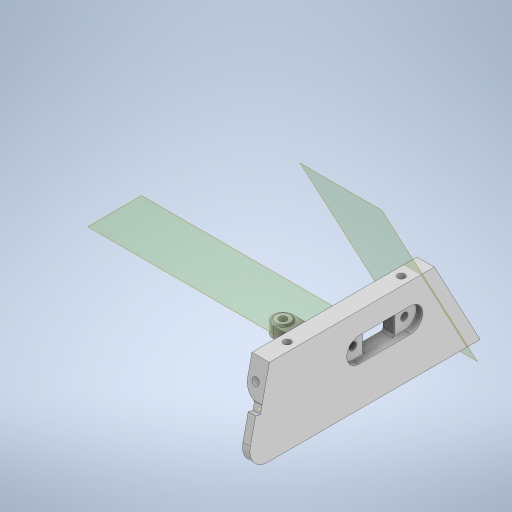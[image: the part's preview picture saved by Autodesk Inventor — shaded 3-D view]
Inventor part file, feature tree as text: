
AUTODESK INVENTOR PART (.ipt)
format: ipt  version: 2023 (Build 270158000, 158)  size: 820,224 bytes
history: native  units: mm
features: extrude x31, sketch x31, reference x17, other x16, projected_geometry x16, fillet x9, chamfer x1
ambient origin geometry x8: Origin, YZ Plane, XZ Plane, XY Plane, X Axis, Y Axis, Z Axis, Center Point
bodies: Body1 (feature_tree)
feature tree (121):
  other  "Bryła1"
  extrude  "Wyciągnięcie proste1"  Depth=6.5mm TaperAngle=0.0deg
  extrude  "Wyciągnięcie proste2"  Depth=3.7mm TaperAngle=0.0deg
  extrude  "Wyciągnięcie proste3"  Depth=1.5mm TaperAngle=0.0deg
  extrude  "Wyciągnięcie proste4"  Depth=6.0mm
  extrude  "Wyciągnięcie proste5"  Depth=3.0mm TaperAngle=0.0deg
  extrude  "Wyciągnięcie proste6"  Depth=5.0mm
  extrude  "Wyciągnięcie proste7"  Depth=3.0mm
  fillet  "Zaokrąglenie1"  Radius=15.0mm
  extrude  "Wyciągnięcie proste8"  Depth=6.0mm
  fillet  "Zaokrąglenie2"  Radius=15.0mm
  fillet  "Zaokrąglenie3"  Radius=35.5mm
  extrude  "Wyciągnięcie proste9"  TaperAngle=0.0deg  [1 undecoded]
  other  "Płaszczyzna konstrukcyjna1"
  extrude  "Wyciągnięcie proste12"  Depth=5.0mm
  extrude  "Wyciągnięcie proste13"  Depth=10.0mm TaperAngle=0.0deg
  other  "Płaszczyzna konstrukcyjna2"
  extrude  "Wyciągnięcie proste14"  Depth=3.5mm
  extrude  "Wyciągnięcie proste15"  Depth=2.0mm
  chamfer  "Faza1"  Distance=7.22mm
  fillet  "Zaokrąglenie7"  Radius=3.0mm
  fillet  "Zaokrąglenie8"  Radius=15.0mm
  fillet  "Zaokrąglenie9"  [1 undecoded]
  extrude  "Wyciągnięcie proste16"  Depth=10.0mm
  extrude  "Wyciągnięcie proste17"  Depth=10.0mm
  fillet  "Zaokrąglenie10"  Radius=7.0mm
  sketch  "Szkic18"
  other  "Płaszczyzna konstrukcyjna3"
  extrude  "Wyciągnięcie proste18"  Depth=7.0mm TaperAngle=0.0deg
  sketch  "Szkic19"
  extrude  "Wyciągnięcie proste19"  Depth=8.0mm
  extrude  "Wyciągnięcie proste20"  Depth=5.0mm TaperAngle=0.0deg
  fillet  "Zaokrąglenie11"  Radius=7.0mm
  extrude  "Wyciągnięcie proste21"  Depth=0.5mm TaperAngle=0.0deg
  extrude  "Wyciągnięcie proste22"  Depth=2.0mm TaperAngle=45.0deg
  extrude  "Wyciągnięcie proste23"  Depth=3.5mm
  sketch  "Szkic25"
  extrude  "Wyciągnięcie proste24"  Depth=2.0mm
  extrude  "Wyciągnięcie proste25"  Depth=4.0mm
  extrude  "Wyciągnięcie proste26"  Depth=10.0mm TaperAngle=0.0deg
  fillet  "Zaokrąglenie12"  Radius=13.0mm
  extrude  "Wyciągnięcie proste27"  Depth=10.0mm
  extrude  "Wyciągnięcie proste28"  TaperAngle=0.0deg  [1 undecoded]
  other  "Płaszczyzna konstrukcyjna4"
  extrude  "Wyciągnięcie proste29"  Depth=1.0mm
  extrude  "Wyciągnięcie proste30"  Depth=10.0mm TaperAngle=0.0deg
  extrude  "Wyciągnięcie proste31"  Depth=3.0mm TaperAngle=0.0deg
  extrude  "Wyciągnięcie proste32"  Depth=3.0mm
  extrude  "Wyciągnięcie proste33"  Depth=3.0mm TaperAngle=0.0deg
  sketch  "Szkic1"
  sketch  "Szkic2"
  sketch  "Szkic3"
  sketch  "Szkic4"
  sketch  "Szkic5"
  sketch  "Szkic6"
  projected_geometry  "Pętla rzutowana1"
  sketch  "Szkic7"
  sketch  "Szkic8"
  projected_geometry  "Pętla rzutowana2"
  sketch  "Szkic9"
  sketch  "Szkic12"
  reference  "Odniesienie1"
  reference  "Odniesienie2"
  sketch  "Szkic13"
  sketch  "Szkic14"
  reference  "Odniesienie3"
  sketch  "Szkic15"
  projected_geometry  "Pętla rzutowana3"
  sketch  "Szkic16"
  projected_geometry  "Pętla rzutowana4"
  sketch  "Szkic17"
  reference  "Odniesienie4"
  reference  "Odniesienie5"
  reference  "Odniesienie6"
  reference  "Odniesienie7"
  projected_geometry  "Pętla rzutowana5"
  sketch  "Szkic20"
  projected_geometry  "Pętla rzutowana6"
  reference  "Odniesienie8"
  sketch  "Szkic21"
  projected_geometry  "Pętla rzutowana7"
  sketch  "Szkic22"
  projected_geometry  "Pętla rzutowana8"
  reference  "Odniesienie9"
  reference  "Odniesienie10"
  sketch  "Szkic23"
  sketch  "Szkic24"
  projected_geometry  "Pętla rzutowana9"
  sketch  "Szkic26"
  projected_geometry  "Pętla rzutowana10"
  reference  "Odniesienie11"
  sketch  "Szkic27"
  reference  "Odniesienie12"
  reference  "Odniesienie13"
  reference  "Odniesienie14"
  reference  "Odniesienie15"
  sketch  "Szkic28"
  reference  "Odniesienie16"
  reference  "Odniesienie17"
  sketch  "Szkic29"
  projected_geometry  "Pętla rzutowana11"
  projected_geometry  "Pętla rzutowana12"
  projected_geometry  "Pętla rzutowana13"
  sketch  "Szkic30"
  sketch  "Szkic31"
  projected_geometry  "Pętla rzutowana14"
  projected_geometry  "Pętla rzutowana15"
  sketch  "Szkic32"
  projected_geometry  "Pętla rzutowana16"
  sketch  "Szkic33"
  other  "<userpath>\Desktop\MojeRoboty\Stefan\mechanics 2\STEFAN.iam"
  other  "STEFAN.iam"
  other  "plytka_dol:1"
  other  "ARDUINO_NANO:1"
  other  "board_up:1"
  other  "koło_minisumo:2"
  other  "podstawa:1"
  other  "plug_2:1"
  other  "tylna:1"
  other  "mocowanie sharpow:1"
  other  "plug_kopia:1"
note: 3 required parameter values undecoded (feature->parameter linkage not recoverable at this tier; creation-order binding heuristic only, values carry confidence <= 0.55)
